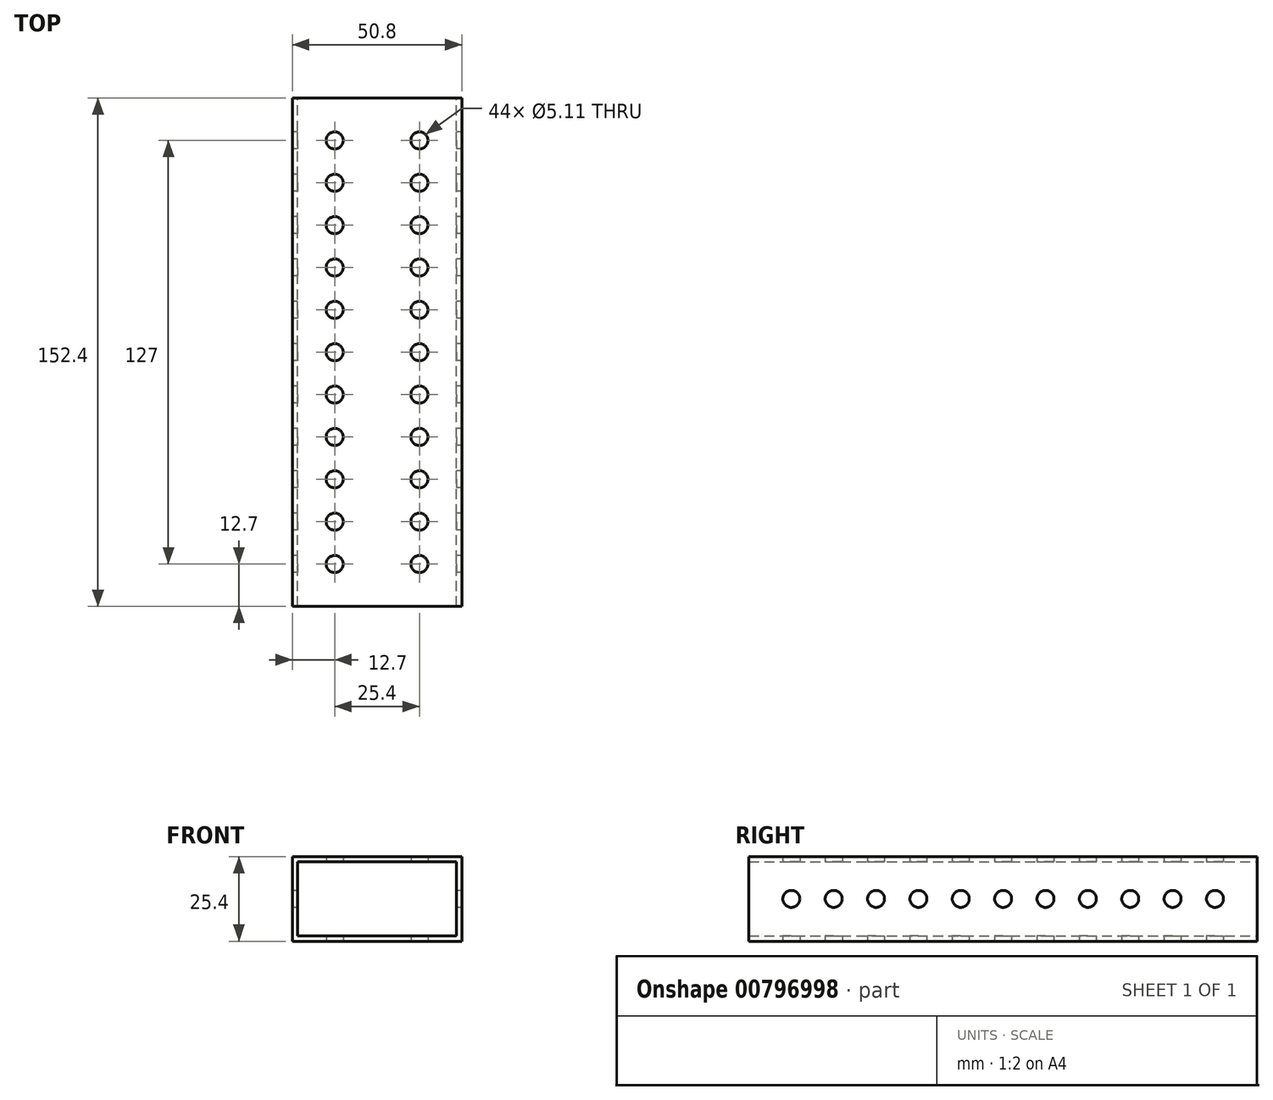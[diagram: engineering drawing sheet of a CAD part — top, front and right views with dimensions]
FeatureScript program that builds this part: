
annotation { "Feature Type Name" : "Feature", "Feature Type Description" : "" }
export const myFeature = defineFeature(function(context is Context, id is Id, definition is map)
    precondition{}
    {
        {
            var Q0;
            Q0=qCreatedBy(makeId("Front.planeOp"),FACE);
            var sketch = newSketch(context, id + "F0", { "sketchPlane" : qUnion([Q0])});
            skLineSegment(sketch, "E0.bottom", {"start": v(-25.4, 12.7) * mm, "end": v(25.4, 12.7) * mm});
            skLineSegment(sketch, "E0.top", {"start": v(-25.4, -12.7) * mm, "end": v(25.4, -12.7) * mm});
            skLineSegment(sketch, "E0.left", {"start": v(-25.4, 12.7) * mm, "end": v(-25.4, -12.7) * mm});
            skLineSegment(sketch, "E0.right", {"start": v(25.4, 12.7) * mm, "end": v(25.4, -12.7) * mm});
            skPoint(sketch, "E0.middle", {"position": v(0, 0) * mm});
            skLineSegment(sketch, "E1.0", {"start": v(-23.81, -11.11) * mm, "end": v(23.81, -11.11) * mm});
            skLineSegment(sketch, "E1.1", {"start": v(-23.81, 11.11) * mm, "end": v(-23.81, -11.11) * mm});
            skLineSegment(sketch, "E1.2", {"start": v(-23.81, 11.11) * mm, "end": v(23.81, 11.11) * mm});
            skLineSegment(sketch, "E1.3", {"start": v(23.81, 11.11) * mm, "end": v(23.81, -11.11) * mm});
            skSolve(sketch);
        }
        {
            var Q0;
            Q0=qSketchRegion(id+"F0",true);
            extrude(context, id + "F1", {"entities" : qUnion([Q0]), "depth" : 152.4 * mm, "offsetDistance" : 25.4 * mm});
        }
        {
            var Q0;
            Q0=makeQuery(id+"F1.opExtrude","SWEPT_FACE",FACE,{"disambiguationData":[OSD([sQuery(id+"F0.wireOp",EDGE,"E0.left")])]});
            var sketch = newSketch(context, id + "F2", { "sketchPlane" : qUnion([Q0])});
            skCircle(sketch, "E2", {"center": v(139.7, 0) * mm, "radius": 2.55 * mm});
            skCircle(sketch, "E3.1.0.0", {"center": v(127, 0) * mm, "radius": 2.55 * mm});
            skCircle(sketch, "E3.2.0.0", {"center": v(114.3, 0) * mm, "radius": 2.55 * mm});
            skCircle(sketch, "E3.3.0.0", {"center": v(101.6, 0) * mm, "radius": 2.55 * mm});
            skCircle(sketch, "E3.4.0.0", {"center": v(88.9, 0) * mm, "radius": 2.55 * mm});
            skCircle(sketch, "E3.5.0.0", {"center": v(76.2, 0) * mm, "radius": 2.55 * mm});
            skCircle(sketch, "E3.6.0.0", {"center": v(63.5, 0) * mm, "radius": 2.55 * mm});
            skLineSegment(sketch, "E3.direction1", {"start": v(139.7, 0) * mm, "end": v(127, 0) * mm, "construction": true});
            skCircle(sketch, "E4.0.7.0", {"center": v(50.8, 0) * mm, "radius": 2.55 * mm});
            skCircle(sketch, "E5.0.8.0", {"center": v(38.1, 0) * mm, "radius": 2.55 * mm});
            skCircle(sketch, "E6.0.9.0", {"center": v(25.4, 0) * mm, "radius": 2.55 * mm});
            skCircle(sketch, "E7.0.10.0", {"center": v(12.7, 0) * mm, "radius": 2.55 * mm});
            skLineSegment(sketch, "E8.bottom", {"start": v(0, 12.7) * mm, "end": v(152.4, 12.7) * mm});
            skLineSegment(sketch, "E8.top", {"start": v(0, -12.7) * mm, "end": v(152.4, -12.7) * mm});
            skLineSegment(sketch, "E8.left", {"start": v(0, 12.7) * mm, "end": v(0, -12.7) * mm});
            skLineSegment(sketch, "E8.right", {"start": v(152.4, 12.7) * mm, "end": v(152.4, -12.7) * mm});
            skSolve(sketch);
        }
        {
            var Q0;
            Q0=makeQuery(id+"F2.imprint","IMPRINT",FACE,{"disambiguationData":[TD([[makeQuery(id+"F2.imprint","IMPRINT",EDGE,{"derivedFrom":sQuery(id+"F2.wireOp",EDGE,"E2")}),1.0]])]});
            var Q1;
            Q1=makeQuery(id+"F2.imprint","IMPRINT",FACE,{"disambiguationData":[TD([[makeQuery(id+"F2.imprint","IMPRINT",EDGE,{"derivedFrom":sQuery(id+"F2.wireOp",EDGE,"E3.2.0.0")}),1.0]])]});
            var Q2;
            Q2=makeQuery(id+"F2.imprint","IMPRINT",FACE,{"disambiguationData":[TD([[makeQuery(id+"F2.imprint","IMPRINT",EDGE,{"derivedFrom":sQuery(id+"F2.wireOp",EDGE,"E6.0.9.0")}),1.0]])]});
            var Q3;
            Q3=makeQuery(id+"F2.imprint","IMPRINT",FACE,{"disambiguationData":[TD([[makeQuery(id+"F2.imprint","IMPRINT",EDGE,{"derivedFrom":sQuery(id+"F2.wireOp",EDGE,"352ad5b7-8d8b-4bdf-98a3-19684e4b1d56.0.11.0")}),1.0]])]});
            var Q4;
            Q4=makeQuery(id+"F2.imprint","IMPRINT",FACE,{"disambiguationData":[TD([[makeQuery(id+"F2.imprint","IMPRINT",EDGE,{"derivedFrom":sQuery(id+"F2.wireOp",EDGE,"E3.3.0.0")}),1.0]])]});
            var Q5;
            Q5=makeQuery(id+"F2.imprint","IMPRINT",FACE,{"disambiguationData":[TD([[makeQuery(id+"F2.imprint","IMPRINT",EDGE,{"derivedFrom":sQuery(id+"F2.wireOp",EDGE,"E3.4.0.0")}),1.0]])]});
            var Q6;
            Q6=makeQuery(id+"F2.imprint","IMPRINT",FACE,{"disambiguationData":[TD([[makeQuery(id+"F2.imprint","IMPRINT",EDGE,{"derivedFrom":sQuery(id+"F2.wireOp",EDGE,"E3.1.0.0")}),1.0]])]});
            var Q7;
            Q7=makeQuery(id+"F2.imprint","IMPRINT",FACE,{"disambiguationData":[TD([[makeQuery(id+"F2.imprint","IMPRINT",EDGE,{"derivedFrom":sQuery(id+"F2.wireOp",EDGE,"E3.6.0.0")}),1.0]])]});
            var Q8;
            Q8=makeQuery(id+"F2.imprint","IMPRINT",FACE,{"disambiguationData":[TD([[makeQuery(id+"F2.imprint","IMPRINT",EDGE,{"derivedFrom":sQuery(id+"F2.wireOp",EDGE,"E3.5.0.0")}),1.0]])]});
            var Q9;
            Q9=makeQuery(id+"F2.imprint","IMPRINT",FACE,{"disambiguationData":[TD([[makeQuery(id+"F2.imprint","IMPRINT",EDGE,{"derivedFrom":sQuery(id+"F2.wireOp",EDGE,"E7.0.10.0")}),1.0]])]});
            var Q10;
            Q10=makeQuery(id+"F2.imprint","IMPRINT",FACE,{"disambiguationData":[TD([[makeQuery(id+"F2.imprint","IMPRINT",EDGE,{"derivedFrom":sQuery(id+"F2.wireOp",EDGE,"E5.0.8.0")}),1.0]])]});
            var Q11;
            Q11=makeQuery(id+"F2.imprint","IMPRINT",FACE,{"disambiguationData":[TD([[makeQuery(id+"F2.imprint","IMPRINT",EDGE,{"derivedFrom":sQuery(id+"F2.wireOp",EDGE,"E4.0.7.0")}),1.0]])]});
            var Q12;
            Q12=makeQuery(id+"F2.imprint","IMPRINT",FACE,{"disambiguationData":[TD([[makeQuery(id+"F2.imprint","IMPRINT",EDGE,{"derivedFrom":sQuery(id+"F2.wireOp",EDGE,"efe4446e-eede-4e7d-b796-4cec8a50af3d.0.12.0")}),1.0]])]});
            extrude(context, id + "F3", {"entities" : qUnion([Q0, Q1, Q2, Q3, Q4, Q5, Q6, Q7, Q8, Q9, Q10, Q11, Q12]), "operationType" : NewBodyOperationType.REMOVE, "oppositeDirection" : true, "depth" : 50.8 * mm, "offsetDistance" : 25.4 * mm});
        }
        {
            var Q0;
            Q0=makeQuery(id+"F1.opExtrude","SWEPT_FACE",FACE,{"disambiguationData":[OSD([sQuery(id+"F0.wireOp",EDGE,"E0.top")])]});
            var sketch = newSketch(context, id + "F4", { "sketchPlane" : qUnion([Q0])});
            skCircle(sketch, "E9", {"center": v(-12.7, 139.7) * mm, "radius": 2.55 * mm});
            skCircle(sketch, "E10.0.1.0", {"center": v(-12.7, 127) * mm, "radius": 2.55 * mm});
            skCircle(sketch, "E10.0.2.0", {"center": v(-12.7, 114.3) * mm, "radius": 2.55 * mm});
            skCircle(sketch, "E10.0.3.0", {"center": v(-12.7, 101.6) * mm, "radius": 2.55 * mm});
            skCircle(sketch, "E10.0.4.0", {"center": v(-12.7, 88.9) * mm, "radius": 2.55 * mm});
            skCircle(sketch, "E10.0.5.0", {"center": v(-12.7, 76.2) * mm, "radius": 2.55 * mm});
            skCircle(sketch, "E10.0.6.0", {"center": v(-12.7, 63.5) * mm, "radius": 2.55 * mm});
            skCircle(sketch, "E10.0.7.0", {"center": v(-12.7, 50.8) * mm, "radius": 2.55 * mm});
            skCircle(sketch, "E10.0.8.0", {"center": v(-12.7, 38.1) * mm, "radius": 2.55 * mm});
            skCircle(sketch, "E10.0.9.0", {"center": v(-12.7, 25.4) * mm, "radius": 2.55 * mm});
            skCircle(sketch, "E10.0.10.0", {"center": v(-12.7, 12.7) * mm, "radius": 2.55 * mm});
            skCircle(sketch, "E10.1.0.0", {"center": v(12.7, 139.7) * mm, "radius": 2.55 * mm});
            skCircle(sketch, "E10.1.1.0", {"center": v(12.7, 127) * mm, "radius": 2.55 * mm});
            skCircle(sketch, "E10.1.2.0", {"center": v(12.7, 114.3) * mm, "radius": 2.55 * mm});
            skCircle(sketch, "E10.1.3.0", {"center": v(12.7, 101.6) * mm, "radius": 2.55 * mm});
            skCircle(sketch, "E10.1.4.0", {"center": v(12.7, 88.9) * mm, "radius": 2.55 * mm});
            skCircle(sketch, "E10.1.5.0", {"center": v(12.7, 76.2) * mm, "radius": 2.55 * mm});
            skCircle(sketch, "E10.1.6.0", {"center": v(12.7, 63.5) * mm, "radius": 2.55 * mm});
            skCircle(sketch, "E10.1.7.0", {"center": v(12.7, 50.8) * mm, "radius": 2.55 * mm});
            skCircle(sketch, "E10.1.8.0", {"center": v(12.7, 38.1) * mm, "radius": 2.55 * mm});
            skCircle(sketch, "E10.1.9.0", {"center": v(12.7, 25.4) * mm, "radius": 2.55 * mm});
            skCircle(sketch, "E10.1.10.0", {"center": v(12.7, 12.7) * mm, "radius": 2.55 * mm});
            skLineSegment(sketch, "E10.direction1", {"start": v(-12.7, 139.7) * mm, "end": v(12.7, 139.7) * mm, "construction": true});
            skLineSegment(sketch, "E10.direction2", {"start": v(-12.7, 139.7) * mm, "end": v(-12.7, 127) * mm, "construction": true});
            skLineSegment(sketch, "E11.bottom", {"start": v(-25.4, 152.4) * mm, "end": v(25.4, 152.4) * mm});
            skLineSegment(sketch, "E11.top", {"start": v(-25.4, 0) * mm, "end": v(25.4, 0) * mm});
            skLineSegment(sketch, "E11.left", {"start": v(-25.4, 152.4) * mm, "end": v(-25.4, 0) * mm});
            skLineSegment(sketch, "E11.right", {"start": v(25.4, 152.4) * mm, "end": v(25.4, 0) * mm});
            skSolve(sketch);
        }
        {
            var Q0;
            Q0=makeQuery(id+"F4.imprint","IMPRINT",FACE,{"disambiguationData":[TD([[makeQuery(id+"F4.imprint","IMPRINT",EDGE,{"derivedFrom":sQuery(id+"F4.wireOp",EDGE,"E10.1.2.0")}),1.0]])]});
            var Q1;
            Q1=makeQuery(id+"F4.imprint","IMPRINT",FACE,{"disambiguationData":[TD([[makeQuery(id+"F4.imprint","IMPRINT",EDGE,{"derivedFrom":sQuery(id+"F4.wireOp",EDGE,"E10.0.10.0")}),1.0]])]});
            var Q2;
            Q2=makeQuery(id+"F4.imprint","IMPRINT",FACE,{"disambiguationData":[TD([[makeQuery(id+"F4.imprint","IMPRINT",EDGE,{"derivedFrom":sQuery(id+"F4.wireOp",EDGE,"E10.1.5.0")}),1.0]])]});
            var Q3;
            Q3=makeQuery(id+"F4.imprint","IMPRINT",FACE,{"disambiguationData":[TD([[makeQuery(id+"F4.imprint","IMPRINT",EDGE,{"derivedFrom":sQuery(id+"F4.wireOp",EDGE,"E10.0.9.0")}),1.0]])]});
            var Q4;
            Q4=makeQuery(id+"F4.imprint","IMPRINT",FACE,{"disambiguationData":[TD([[makeQuery(id+"F4.imprint","IMPRINT",EDGE,{"derivedFrom":sQuery(id+"F4.wireOp",EDGE,"E10.1.0.0")}),1.0]])]});
            var Q5;
            Q5=makeQuery(id+"F4.imprint","IMPRINT",FACE,{"disambiguationData":[TD([[makeQuery(id+"F4.imprint","IMPRINT",EDGE,{"derivedFrom":sQuery(id+"F4.wireOp",EDGE,"E10.1.7.0")}),1.0]])]});
            var Q6;
            Q6=makeQuery(id+"F4.imprint","IMPRINT",FACE,{"disambiguationData":[TD([[makeQuery(id+"F4.imprint","IMPRINT",EDGE,{"derivedFrom":sQuery(id+"F4.wireOp",EDGE,"E10.0.3.0")}),1.0]])]});
            var Q7;
            Q7=makeQuery(id+"F4.imprint","IMPRINT",FACE,{"disambiguationData":[TD([[makeQuery(id+"F4.imprint","IMPRINT",EDGE,{"derivedFrom":sQuery(id+"F4.wireOp",EDGE,"E10.0.11.0")}),1.0]])]});
            var Q8;
            Q8=makeQuery(id+"F4.imprint","IMPRINT",FACE,{"disambiguationData":[TD([[makeQuery(id+"F4.imprint","IMPRINT",EDGE,{"derivedFrom":sQuery(id+"F4.wireOp",EDGE,"E10.1.12.0")}),1.0]])]});
            var Q9;
            Q9=makeQuery(id+"F4.imprint","IMPRINT",FACE,{"disambiguationData":[TD([[makeQuery(id+"F4.imprint","IMPRINT",EDGE,{"derivedFrom":sQuery(id+"F4.wireOp",EDGE,"E10.0.7.0")}),1.0]])]});
            var Q10;
            Q10=makeQuery(id+"F4.imprint","IMPRINT",FACE,{"disambiguationData":[TD([[makeQuery(id+"F4.imprint","IMPRINT",EDGE,{"derivedFrom":sQuery(id+"F4.wireOp",EDGE,"E10.1.3.0")}),1.0]])]});
            var Q11;
            Q11=makeQuery(id+"F4.imprint","IMPRINT",FACE,{"disambiguationData":[TD([[makeQuery(id+"F4.imprint","IMPRINT",EDGE,{"derivedFrom":sQuery(id+"F4.wireOp",EDGE,"E10.1.10.0")}),1.0]])]});
            var Q12;
            Q12=makeQuery(id+"F4.imprint","IMPRINT",FACE,{"disambiguationData":[TD([[makeQuery(id+"F4.imprint","IMPRINT",EDGE,{"derivedFrom":sQuery(id+"F4.wireOp",EDGE,"E10.1.4.0")}),1.0]])]});
            var Q13;
            Q13=makeQuery(id+"F4.imprint","IMPRINT",FACE,{"disambiguationData":[TD([[makeQuery(id+"F4.imprint","IMPRINT",EDGE,{"derivedFrom":sQuery(id+"F4.wireOp",EDGE,"E10.0.1.0")}),1.0]])]});
            var Q14;
            Q14=makeQuery(id+"F4.imprint","IMPRINT",FACE,{"disambiguationData":[TD([[makeQuery(id+"F4.imprint","IMPRINT",EDGE,{"derivedFrom":sQuery(id+"F4.wireOp",EDGE,"E10.1.1.0")}),1.0]])]});
            var Q15;
            Q15=makeQuery(id+"F4.imprint","IMPRINT",FACE,{"disambiguationData":[TD([[makeQuery(id+"F4.imprint","IMPRINT",EDGE,{"derivedFrom":sQuery(id+"F4.wireOp",EDGE,"E10.0.5.0")}),1.0]])]});
            var Q16;
            Q16=makeQuery(id+"F4.imprint","IMPRINT",FACE,{"disambiguationData":[TD([[makeQuery(id+"F4.imprint","IMPRINT",EDGE,{"derivedFrom":sQuery(id+"F4.wireOp",EDGE,"E9")}),1.0]])]});
            var Q17;
            Q17=makeQuery(id+"F4.imprint","IMPRINT",FACE,{"disambiguationData":[TD([[makeQuery(id+"F4.imprint","IMPRINT",EDGE,{"derivedFrom":sQuery(id+"F4.wireOp",EDGE,"E10.0.4.0")}),1.0]])]});
            var Q18;
            Q18=makeQuery(id+"F4.imprint","IMPRINT",FACE,{"disambiguationData":[TD([[makeQuery(id+"F4.imprint","IMPRINT",EDGE,{"derivedFrom":sQuery(id+"F4.wireOp",EDGE,"E10.0.8.0")}),1.0]])]});
            var Q19;
            Q19=makeQuery(id+"F4.imprint","IMPRINT",FACE,{"disambiguationData":[TD([[makeQuery(id+"F4.imprint","IMPRINT",EDGE,{"derivedFrom":sQuery(id+"F4.wireOp",EDGE,"E10.1.8.0")}),1.0]])]});
            var Q20;
            Q20=makeQuery(id+"F4.imprint","IMPRINT",FACE,{"disambiguationData":[TD([[makeQuery(id+"F4.imprint","IMPRINT",EDGE,{"derivedFrom":sQuery(id+"F4.wireOp",EDGE,"E10.0.12.0")}),1.0]])]});
            var Q21;
            Q21=makeQuery(id+"F4.imprint","IMPRINT",FACE,{"disambiguationData":[TD([[makeQuery(id+"F4.imprint","IMPRINT",EDGE,{"derivedFrom":sQuery(id+"F4.wireOp",EDGE,"E10.1.6.0")}),1.0]])]});
            var Q22;
            Q22=makeQuery(id+"F4.imprint","IMPRINT",FACE,{"disambiguationData":[TD([[makeQuery(id+"F4.imprint","IMPRINT",EDGE,{"derivedFrom":sQuery(id+"F4.wireOp",EDGE,"E10.1.11.0")}),1.0]])]});
            var Q23;
            Q23=makeQuery(id+"F4.imprint","IMPRINT",FACE,{"disambiguationData":[TD([[makeQuery(id+"F4.imprint","IMPRINT",EDGE,{"derivedFrom":sQuery(id+"F4.wireOp",EDGE,"E10.0.2.0")}),1.0]])]});
            var Q24;
            Q24=makeQuery(id+"F4.imprint","IMPRINT",FACE,{"disambiguationData":[TD([[makeQuery(id+"F4.imprint","IMPRINT",EDGE,{"derivedFrom":sQuery(id+"F4.wireOp",EDGE,"E10.0.6.0")}),1.0]])]});
            var Q25;
            Q25=makeQuery(id+"F4.imprint","IMPRINT",FACE,{"disambiguationData":[TD([[makeQuery(id+"F4.imprint","IMPRINT",EDGE,{"derivedFrom":sQuery(id+"F4.wireOp",EDGE,"E10.1.9.0")}),1.0]])]});
            extrude(context, id + "F5", {"entities" : qUnion([Q0, Q1, Q2, Q3, Q4, Q5, Q6, Q7, Q8, Q9, Q10, Q11, Q12, Q13, Q14, Q15, Q16, Q17, Q18, Q19, Q20, Q21, Q22, Q23, Q24, Q25]), "operationType" : NewBodyOperationType.REMOVE, "oppositeDirection" : true, "depth" : 254 * mm, "offsetDistance" : 25.4 * mm});
        }
    });
